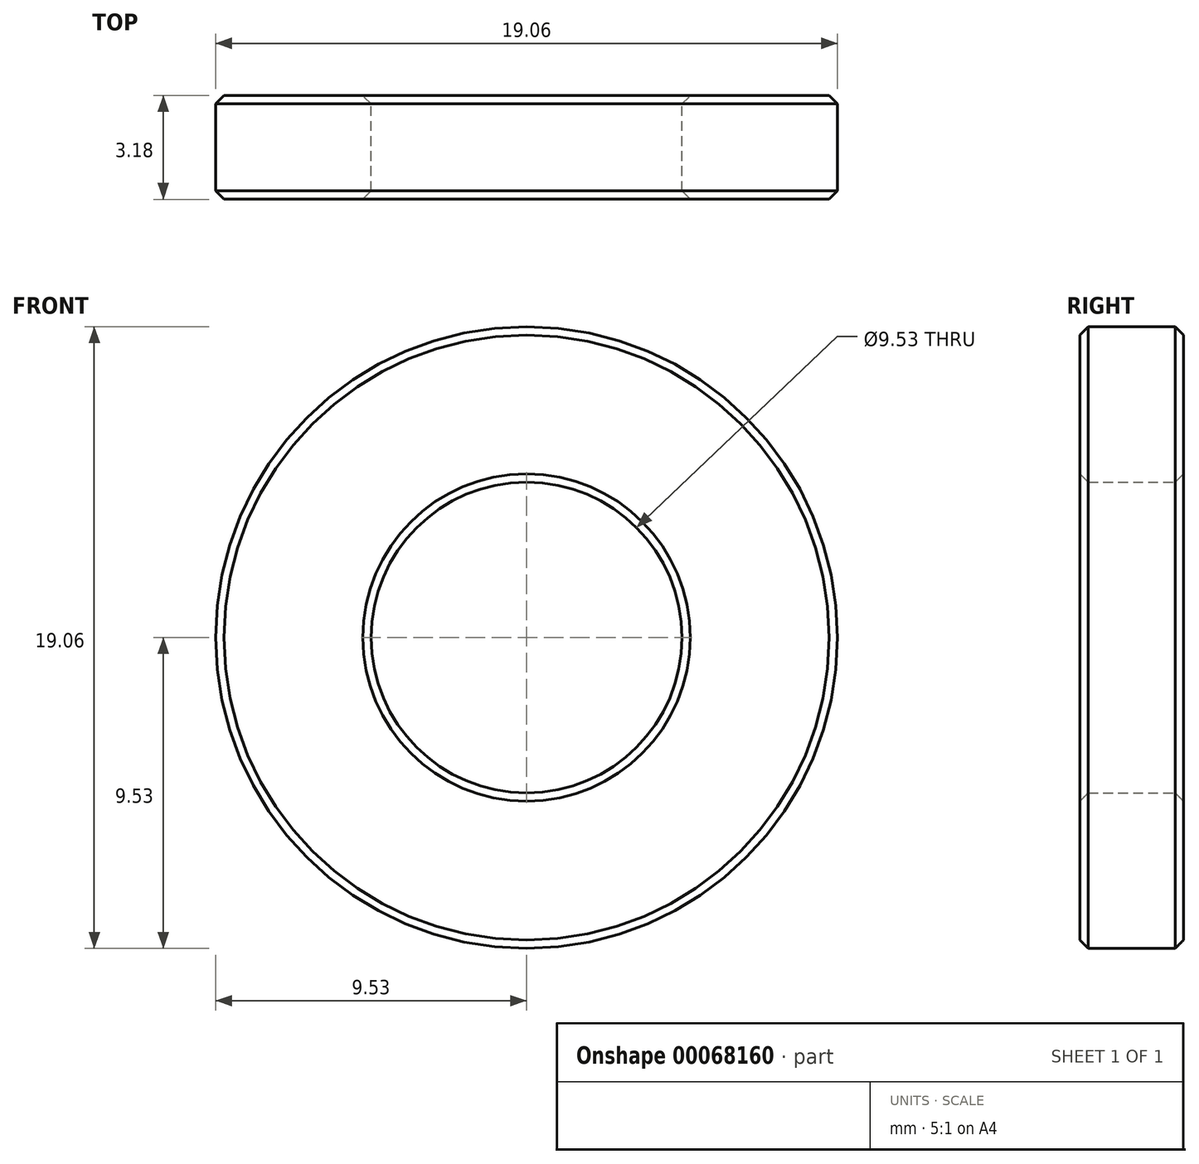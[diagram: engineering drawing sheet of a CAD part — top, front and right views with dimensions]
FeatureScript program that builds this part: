
annotation { "Feature Type Name" : "Feature", "Feature Type Description" : "" }
export const myFeature = defineFeature(function(context is Context, id is Id, definition is map)
    precondition{}
    {
        {
            var Q0;
            Q0=qCreatedBy(makeId("Front.planeOp"),FACE);
            var sketch = newSketch(context, id + "F0", { "sketchPlane" : qUnion([Q0])});
            skCircle(sketch, "E0", {"center": v(0, 0) * mm, "radius": 9.53 * mm});
            skCircle(sketch, "E1", {"center": v(0, 0) * mm, "radius": 4.76 * mm});
            skSolve(sketch);
        }
        {
            var Q0;
            Q0=makeQuery(id+"F0.imprint","IMPRINT",FACE,{"disambiguationData":[TD([[makeQuery(id+"F0.imprint","IMPRINT",EDGE,{"derivedFrom":sQuery(id+"F0.wireOp",EDGE,"E0")}),1.0]])]});
            extrude(context, id + "F1", {"entities" : qUnion([Q0]), "endBound" : BoundingType.SYMMETRIC, "depth" : 3.17 * mm});
        }
        {
            var Q0;
            Q0=makeQuery(id+"F1.opExtrude","CAP_EDGE",EDGE,{"disambiguationData":[OSD([sQuery(id+"F0.wireOp",EDGE,"E0")])],"isStart":false});
            var Q1;
            Q1=makeQuery(id+"F1.opExtrude","CAP_EDGE",EDGE,{"disambiguationData":[OSD([sQuery(id+"F0.wireOp",EDGE,"E0")])],"isStart":true});
            var Q2;
            Q2=makeQuery(id+"F1.opExtrude","CAP_EDGE",EDGE,{"disambiguationData":[OSD([sQuery(id+"F0.wireOp",EDGE,"E1")])],"isStart":false});
            var Q3;
            Q3=makeQuery(id+"F1.opExtrude","CAP_EDGE",EDGE,{"disambiguationData":[OSD([sQuery(id+"F0.wireOp",EDGE,"E1")])],"isStart":true});
            chamfer(context, id + "F2", {"entities" : qUnion([Q0, Q1, Q2, Q3]), "width" : 0.25 * mm, "tangentPropagation" : true});
        }
    });
